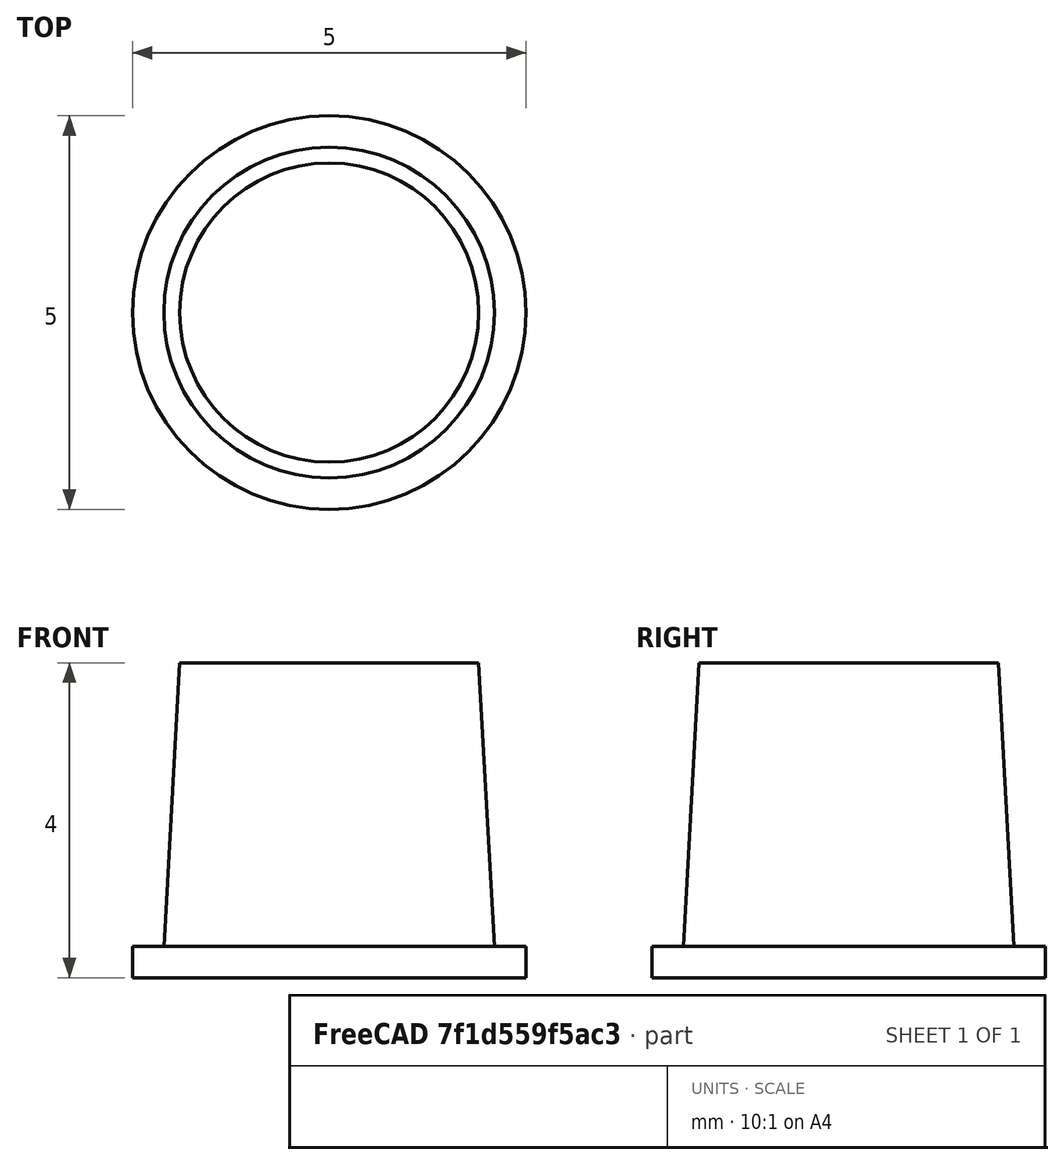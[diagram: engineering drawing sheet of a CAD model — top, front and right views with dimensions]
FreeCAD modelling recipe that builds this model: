
FCSTD DOCUMENT  (FreeCAD 2024.2R37179 (Git))
Label: Fitting
License: All rights reserved
LicenseURL: https://en.wikipedia.org/wiki/All_rights_reserved
objects: Sketcher::SketchObject×1, PartDesign::Revolution×1, PartDesign::Body×1
note: 4 computed .brp shape members not serialized (recipe doc carries the construction recipe); baked Part::Feature solids carry a one-line shape summary decoded from their .brp

FEATURE [Sketcher::SketchObject] Sketch
  AttachmentSupport = -> [XZ_Plane]
  FullyConstrained = true
  MapMode = 5
  Placement = pos=(0,0,0) rot=(1,0,0;1.5708rad)
  sketch-geometry (6):
    g0: LineSegment StartX=-2.5 StartY=0.4 StartZ=0 EndX=-2.5 EndY=0 EndZ=0
    g1: LineSegment StartX=-2.5 StartY=0 StartZ=0 EndX=0 EndY=0 EndZ=0
    g2: LineSegment StartX=0 StartY=0 StartZ=0 EndX=0 EndY=4 EndZ=0
    g3: LineSegment StartX=0 StartY=4 StartZ=0 EndX=-1.9 EndY=4 EndZ=0
    g4: LineSegment StartX=-1.9 StartY=4 StartZ=0 EndX=-2.1 EndY=0.4 EndZ=0
    g5: LineSegment StartX=-2.1 StartY=0.4 StartZ=0 EndX=-2.5 EndY=0.4 EndZ=0
  constraints (17):
    c: PointOnObject(g0,g-1)
    c: Vertical(g0)
    c: Coincident(g0,g1)
    c: Coincident(g1,g-1)
    c: Coincident(g1,g2)
    c: PointOnObject(g2,g-2)
    c: Coincident(g2,g3)
    c: Horizontal(g3)
    c: Coincident(g3,g4)
    c: Coincident(g4,g5)
    c: Coincident(g5,g0)
    c: Horizontal(g5)
    c: DistanceX(g1,g1) = 2.5
    c: DistanceX(g4,g1) = 2.1
    c: Distance(g3,g3) = 1.9
    c: DistanceY(g2,g2) = 4
    c: DistanceY(g0,g0) = 0.4
FEATURE [PartDesign::Revolution] Revolution
  Angle = 360
  Angle2 = 60
  Axis = (0,2e-16,1)
  Base = (0,0,0)
  Placement = pos=(0,0,0) rot=(1,0,0;1.5708rad)
  Profile = -> Sketch
  ReferenceAxis = -> Sketch [V_Axis]
  Refine = true
  Suppressed = false
  Type = 0
FEATURE [PartDesign::Body] Body
  Group = -> [Sketch,Revolution]
  Origin = -> Origin
  Tip = -> Revolution
